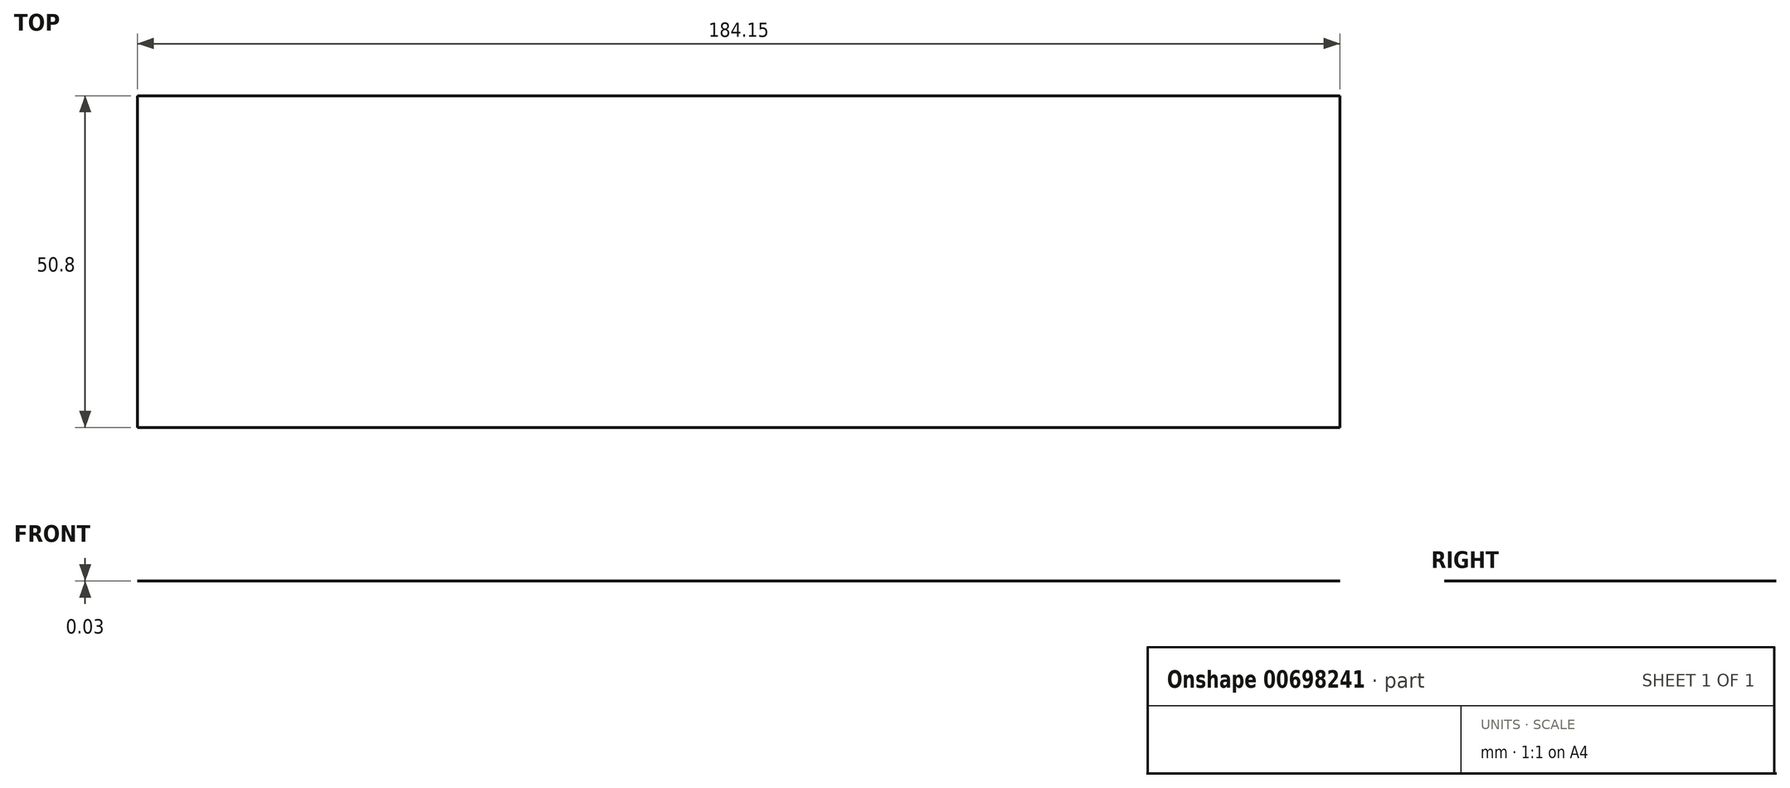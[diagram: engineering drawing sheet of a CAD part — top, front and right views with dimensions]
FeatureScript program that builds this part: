
annotation { "Feature Type Name" : "Feature", "Feature Type Description" : "" }
export const myFeature = defineFeature(function(context is Context, id is Id, definition is map)
    precondition{}
    {
        {
            var Q0;
            Q0=qCreatedBy(makeId("Top.planeOp"),FACE);
            var sketch = newSketch(context, id + "F0", { "sketchPlane" : qUnion([Q0])});
            skLineSegment(sketch, "E0.bottom", {"start": v(-111.86, 60.3) * mm, "end": v(72.3, 60.3) * mm});
            skLineSegment(sketch, "E0.top", {"start": v(-111.86, 9.5) * mm, "end": v(72.3, 9.5) * mm});
            skLineSegment(sketch, "E0.left", {"start": v(-111.86, 60.3) * mm, "end": v(-111.86, 9.5) * mm});
            skLineSegment(sketch, "E0.right", {"start": v(72.3, 60.3) * mm, "end": v(72.3, 9.5) * mm});
            skSolve(sketch);
        }
        {
            var Q0;
            Q0 = qSketchRegion(id + "F0", true);
            extrude(context, id + "F1", {"entities" : qUnion([Q0]), "depth" : 3 / 101.6 * mm, "offsetDistance" : 25.4 * mm});
        }
    });
